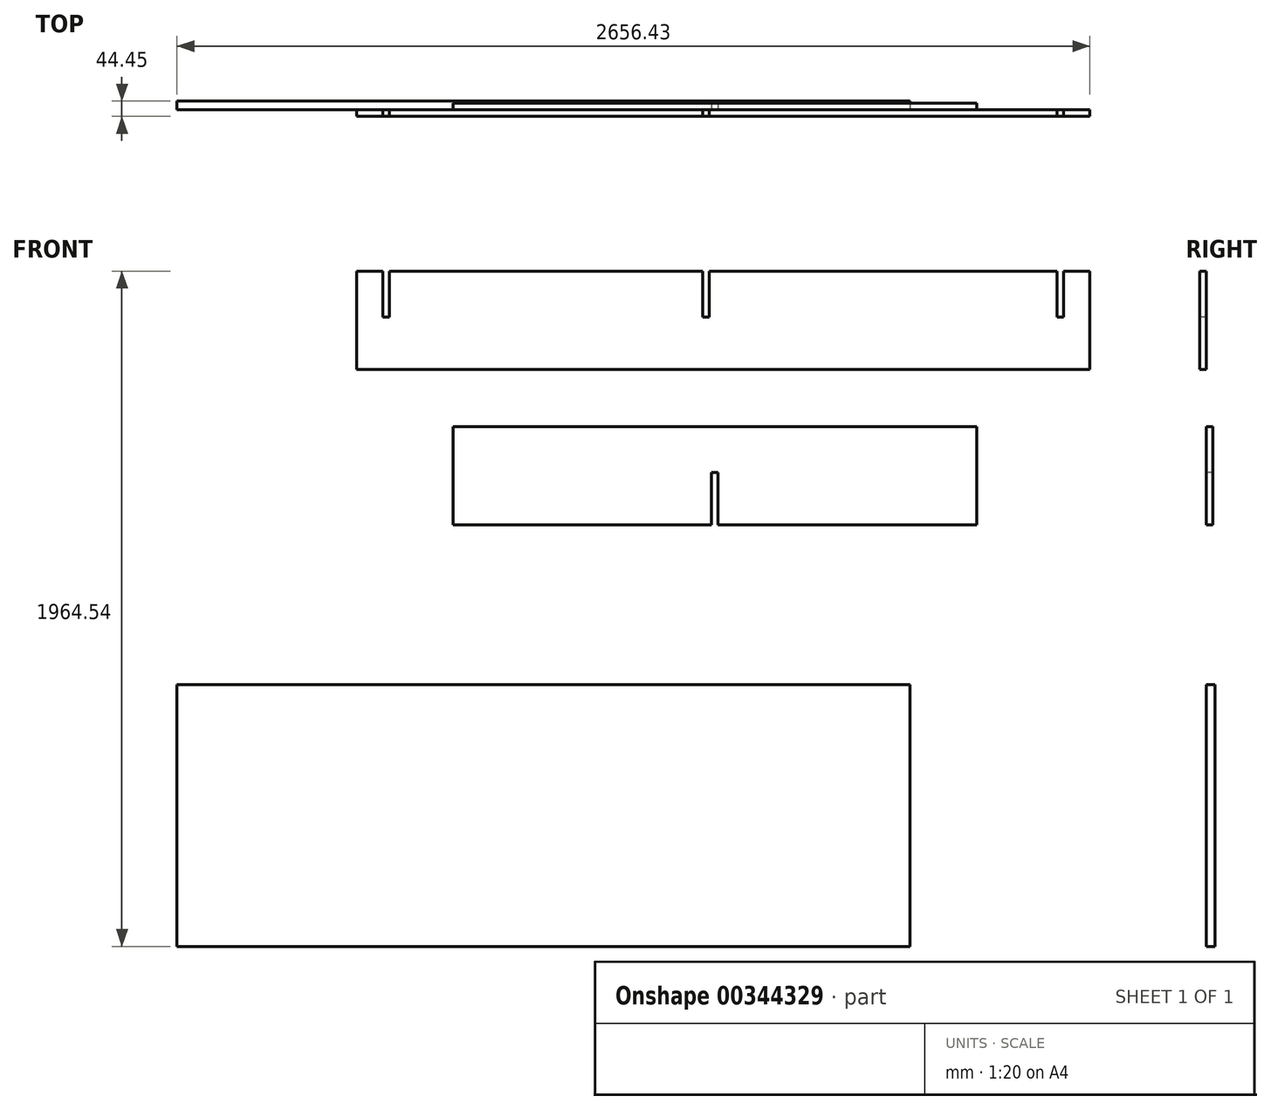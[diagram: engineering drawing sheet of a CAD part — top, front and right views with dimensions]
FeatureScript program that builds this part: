
annotation { "Feature Type Name" : "Feature", "Feature Type Description" : "" }
export const myFeature = defineFeature(function(context is Context, id is Id, definition is map)
    precondition{}
    {
        {
            var Q0;
            Q0=qCreatedBy(makeId("Front.planeOp"),FACE);
            var sketch = newSketch(context, id + "F0", { "sketchPlane" : qUnion([Q0])});
            skLineSegment(sketch, "E0.bottom", {"start": v(-372.5, 127.69) * mm, "end": v(1761.1, 127.69) * mm});
            skLineSegment(sketch, "E0.top", {"start": v(-372.5, -158.06) * mm, "end": v(1761.1, -158.06) * mm});
            skLineSegment(sketch, "E0.left", {"start": v(-372.5, 127.69) * mm, "end": v(-372.5, -158.06) * mm});
            skLineSegment(sketch, "E0.right", {"start": v(1761.1, 127.69) * mm, "end": v(1761.1, -158.06) * mm});
            skSolve(sketch);
        }
        {
            var Q0;
            Q0=makeQuery(id+"F0.imprint","IMPRINT",FACE,{"disambiguationData":[TD([[makeQuery(id+"F0.imprint","IMPRINT",EDGE,{"derivedFrom":sQuery(id+"F0.wireOp",EDGE,"E0.bottom")}),-1.0]])]});
            extrude(context, id + "F1", {"entities" : qUnion([Q0]), "depth" : 19.05 * mm});
        }
        {
            var Q0;
            Q0=makeQuery(id+"F1.opExtrude","CAP_FACE",FACE,{"disambiguationData":[OSD([sQuery(id+"F0.wireOp",EDGE,"E0.bottom"),sQuery(id+"F0.wireOp",EDGE,"E0.top"),sQuery(id+"F0.wireOp",EDGE,"E0.left"),sQuery(id+"F0.wireOp",EDGE,"E0.right")])],"isStart":false});
            var sketch = newSketch(context, id + "F2", { "sketchPlane" : qUnion([Q0])});
            skLineSegment(sketch, "E1.bottom", {"start": v(633.97, 127.69) * mm, "end": v(653.02, 127.69) * mm});
            skLineSegment(sketch, "E1.top", {"start": v(633.97, -5.66) * mm, "end": v(653.02, -5.66) * mm});
            skLineSegment(sketch, "E1.left", {"start": v(633.97, 127.69) * mm, "end": v(633.97, -5.66) * mm});
            skLineSegment(sketch, "E1.right", {"start": v(653.02, 127.69) * mm, "end": v(653.02, -5.66) * mm});
            skLineSegment(sketch, "E2.bottom", {"start": v(-296.3, 127.69) * mm, "end": v(-277.26, 127.69) * mm});
            skLineSegment(sketch, "E2.top", {"start": v(-296.3, -5.66) * mm, "end": v(-277.26, -5.66) * mm});
            skLineSegment(sketch, "E2.left", {"start": v(-296.3, 127.69) * mm, "end": v(-296.3, -5.66) * mm});
            skLineSegment(sketch, "E2.right", {"start": v(-277.26, 127.69) * mm, "end": v(-277.26, -5.66) * mm});
            skLineSegment(sketch, "E3.bottom", {"start": v(1684.9, 127.69) * mm, "end": v(1665.84, 127.69) * mm});
            skLineSegment(sketch, "E3.top", {"start": v(1684.9, -5.66) * mm, "end": v(1665.84, -5.66) * mm});
            skLineSegment(sketch, "E3.left", {"start": v(1684.9, 127.69) * mm, "end": v(1684.9, -5.66) * mm});
            skLineSegment(sketch, "E3.right", {"start": v(1665.84, 127.69) * mm, "end": v(1665.84, -5.66) * mm});
            skSolve(sketch);
        }
        {
            var Q0;
            Q0 = qSketchRegion(id + "F2", true);
            extrude(context, id + "F3", {"entities" : qUnion([Q0]), "operationType" : NewBodyOperationType.REMOVE, "endBound" : BoundingType.THROUGH_ALL, "oppositeDirection" : true, "depth" : 25.4 * mm});
        }
        {
            var Q0;
            Q0=qCreatedBy(makeId("Front.planeOp"),FACE);
            var sketch = newSketch(context, id + "F4", { "sketchPlane" : qUnion([Q0])});
            skLineSegment(sketch, "E4.bottom", {"start": v(-92.33, -324.92) * mm, "end": v(1431.67, -324.92) * mm});
            skLineSegment(sketch, "E4.top", {"start": v(-92.33, -610.67) * mm, "end": v(1431.67, -610.67) * mm});
            skLineSegment(sketch, "E4.left", {"start": v(-92.33, -324.92) * mm, "end": v(-92.33, -610.67) * mm});
            skLineSegment(sketch, "E4.right", {"start": v(1431.67, -324.92) * mm, "end": v(1431.67, -610.67) * mm});
            skSolve(sketch);
        }
        {
            var Q0;
            Q0=makeQuery(id+"F4.imprint","IMPRINT",FACE,{"disambiguationData":[TD([[makeQuery(id+"F4.imprint","IMPRINT",EDGE,{"derivedFrom":sQuery(id+"F4.wireOp",EDGE,"E4.bottom")}),-1.0]])]});
            extrude(context, id + "F5", {"entities" : qUnion([Q0]), "oppositeDirection" : true, "depth" : 19.05 * mm});
        }
        {
            var Q0;
            Q0=makeQuery(id+"F5.opExtrude","CAP_FACE",FACE,{"disambiguationData":[OSD([sQuery(id+"F4.wireOp",EDGE,"E4.bottom"),sQuery(id+"F4.wireOp",EDGE,"E4.top"),sQuery(id+"F4.wireOp",EDGE,"E4.left"),sQuery(id+"F4.wireOp",EDGE,"E4.right")])],"isStart":true});
            var sketch = newSketch(context, id + "F6", { "sketchPlane" : qUnion([Q0])});
            skLineSegment(sketch, "E5.bottom", {"start": v(660.15, -610.67) * mm, "end": v(679.2, -610.67) * mm});
            skLineSegment(sketch, "E5.top", {"start": v(660.15, -458.27) * mm, "end": v(679.2, -458.27) * mm});
            skLineSegment(sketch, "E5.left", {"start": v(660.15, -610.67) * mm, "end": v(660.15, -458.27) * mm});
            skLineSegment(sketch, "E5.right", {"start": v(679.2, -610.67) * mm, "end": v(679.2, -458.27) * mm});
            skSolve(sketch);
        }
        {
            var Q0;
            Q0 = qSketchRegion(id + "F6", true);
            extrude(context, id + "F7", {"entities" : qUnion([Q0]), "operationType" : NewBodyOperationType.REMOVE, "endBound" : BoundingType.THROUGH_ALL, "oppositeDirection" : true, "depth" : 25.4 * mm});
        }
        {
            var Q0;
            Q0=qCreatedBy(makeId("Front.planeOp"),FACE);
            var sketch = newSketch(context, id + "F8", { "sketchPlane" : qUnion([Q0])});
            skLineSegment(sketch, "E6.bottom", {"start": v(-895.34, -1074.85) * mm, "end": v(1238.26, -1074.85) * mm});
            skLineSegment(sketch, "E6.top", {"start": v(-895.34, -1836.85) * mm, "end": v(1238.26, -1836.85) * mm});
            skLineSegment(sketch, "E6.left", {"start": v(-895.34, -1074.85) * mm, "end": v(-895.34, -1836.85) * mm});
            skLineSegment(sketch, "E6.right", {"start": v(1238.26, -1074.85) * mm, "end": v(1238.26, -1836.85) * mm});
            skSolve(sketch);
        }
        {
            var Q0;
            Q0=makeQuery(id+"F8.imprint","IMPRINT",FACE,{"disambiguationData":[TD([[makeQuery(id+"F8.imprint","IMPRINT",EDGE,{"derivedFrom":sQuery(id+"F8.wireOp",EDGE,"E6.bottom")}),-1.0]])]});
            extrude(context, id + "F9", {"entities" : qUnion([Q0]), "oppositeDirection" : true, "depth" : 25.4 * mm});
        }
    });
